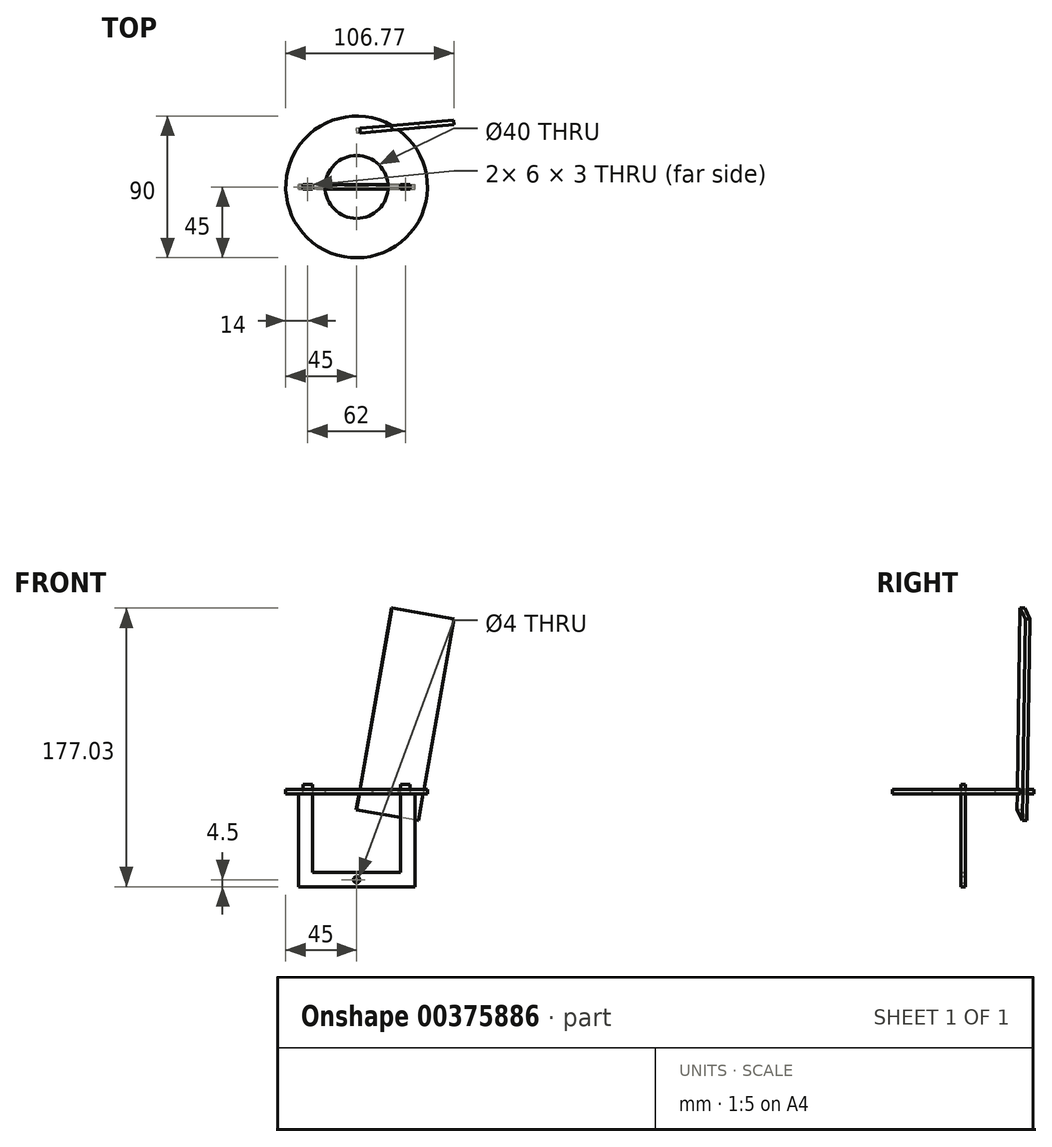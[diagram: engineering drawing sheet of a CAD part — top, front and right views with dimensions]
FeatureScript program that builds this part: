
annotation { "Feature Type Name" : "Feature", "Feature Type Description" : "" }
export const myFeature = defineFeature(function(context is Context, id is Id, definition is map)
    precondition{}
    {
        {
            var Q0;
            Q0=qCreatedBy(makeId("Top.planeOp"),FACE);
            var sketch = newSketch(context, id + "F0", { "sketchPlane" : qUnion([Q0])});
            skCircle(sketch, "E0", {"center": v(0, 0) * mm, "radius": 20 * mm});
            skCircle(sketch, "E1", {"center": v(0, 0) * mm, "radius": 45 * mm});
            skLineSegment(sketch, "E2.bottom", {"start": v(-34, -1.5) * mm, "end": v(-28, -1.5) * mm});
            skLineSegment(sketch, "E2.top", {"start": v(-34, 1.5) * mm, "end": v(-28, 1.5) * mm});
            skLineSegment(sketch, "E2.left", {"start": v(-34, -1.5) * mm, "end": v(-34, 1.5) * mm});
            skLineSegment(sketch, "E2.right", {"start": v(-28, -1.5) * mm, "end": v(-28, 1.5) * mm});
            skPoint(sketch, "E2.middle", {"position": v(-31, 0) * mm});
            skLineSegment(sketch, "E3.MirrorCS", {"start": v(34, -1.5) * mm, "end": v(28, -1.5) * mm});
            skPoint(sketch, "E4.MirrorP", {"position": v(31, 0) * mm});
            skLineSegment(sketch, "E5.MirrorCS", {"start": v(34, -1.5) * mm, "end": v(34, 1.5) * mm});
            skLineSegment(sketch, "E6.MirrorCS", {"start": v(34, 1.5) * mm, "end": v(28, 1.5) * mm});
            skLineSegment(sketch, "E7.MirrorCS", {"start": v(28, -1.5) * mm, "end": v(28, 1.5) * mm});
            skSolve(sketch);
        }
        {
            var Q0;
            Q0=makeQuery(id+"F0.imprint","IMPRINT",FACE,{"disambiguationData":[TD([[makeQuery(id+"F0.imprint","IMPRINT",EDGE,{"derivedFrom":sQuery(id+"F0.wireOp",EDGE,"E0")}),-1.0]])]});
            extrude(context, id + "F1", {"entities" : qUnion([Q0]), "depth" : 3 * mm});
        }
        {
            var Q0;
            Q0=qCreatedBy(makeId("Top.planeOp"),FACE);
            var sketch = newSketch(context, id + "F2", { "sketchPlane" : qUnion([Q0])});
            skLineSegment(sketch, "E8", {"start": v(9.74, 37.99) * mm, "end": v(39.62, 40.6) * mm});
            skLineSegment(sketch, "E9", {"start": v(39.62, 40.6) * mm, "end": v(39.89, 37.61) * mm});
            skLineSegment(sketch, "E10", {"start": v(39.89, 37.61) * mm, "end": v(10, 35) * mm});
            skLineSegment(sketch, "E11", {"start": v(9.74, 37.99) * mm, "end": v(10, 35) * mm});
            skCircle(sketch, "E12.0", {"center": v(0, 0) * mm, "radius": 20 * mm, "construction": true});
            skSolve(sketch);
        }
        {
            var Q0;
            Q0=makeQuery(id+"F2.imprint","IMPRINT",FACE,{"disambiguationData":[TD([[makeQuery(id+"F2.imprint","IMPRINT",EDGE,{"derivedFrom":sQuery(id+"F2.wireOp",EDGE,"E8")}),-1.0]])]});
            extrude(context, id + "F3", {"entities" : qUnion([Q0]), "operationType" : NewBodyOperationType.REMOVE, "depth" : 25 * mm});
        }
        {
            var Q0;
            Q0=makeQuery(id+"F3.boolean.opBoolean","COPY",FACE,{"derivedFrom":makeQuery(id+"F3.opExtrude","SWEPT_FACE",FACE,{"disambiguationData":[OSD([sQuery(id+"F2.wireOp",EDGE,"E10")])]})});
            var sketch = newSketch(context, id + "F4", { "sketchPlane" : qUnion([Q0])});
            skLineSegment(sketch, "E13.bottom", {"start": v(-64.98, 111.08) * mm, "end": v(-25.59, 118.03) * mm});
            skLineSegment(sketch, "E13.top", {"start": v(-42.4, -16.95) * mm, "end": v(-3.01, -10) * mm});
            skLineSegment(sketch, "E13.left", {"start": v(-64.98, 111.08) * mm, "end": v(-42.4, -16.95) * mm});
            skLineSegment(sketch, "E13.right", {"start": v(-25.59, 118.03) * mm, "end": v(-5.3, 3) * mm});
            skLineSegment(sketch, "E14.0", {"start": v(-13.01, 3) * mm, "end": v(-13.01, 0) * mm});
            skLineSegment(sketch, "E15", {"start": v(-13.01, 0) * mm, "end": v(-4.78, 0) * mm});
            skLineSegment(sketch, "E16", {"start": v(-13.01, 3) * mm, "end": v(-5.3, 3) * mm});
            skLineSegment(sketch, "E17.trimOffspring", {"start": v(-4.78, 0) * mm, "end": v(-3.01, -10) * mm});
            skPoint(sketch, "E18", {"position": v(-13.01, -11.76) * mm});
            skSolve(sketch);
        }
        {
            var Q0;
            Q0 = qSketchRegion(id + "F4", true);
            var Q1;
            Q1=makeQuery(id+"F3.boolean.opBoolean","COPY",FACE,{"derivedFrom":makeQuery(id+"F3.opExtrude","SWEPT_FACE",FACE,{"disambiguationData":[OSD([sQuery(id+"F2.wireOp",EDGE,"E8")])]})});
            extrude(context, id + "F5", {"entities" : qUnion([Q0]), "endBoundEntityFace" : qUnion([Q1]), "depth" : 3 * mm});
        }
        {
            var Q0;
            Q0=qCreatedBy(makeId("Front.planeOp"),FACE);
            var sketch = newSketch(context, id + "F6", { "sketchPlane" : qUnion([Q0])});
            skLineSegment(sketch, "E19.0", {"start": v(-34, 3) * mm, "end": v(-34, 0) * mm});
            skLineSegment(sketch, "E20.0", {"start": v(-28, 3) * mm, "end": v(-28, 0) * mm});
            skLineSegment(sketch, "E21", {"start": v(-28, 3) * mm, "end": v(-28, 6) * mm});
            skLineSegment(sketch, "E22", {"start": v(-28, 6) * mm, "end": v(-34, 6) * mm});
            skLineSegment(sketch, "E23", {"start": v(-34, 3) * mm, "end": v(-34, 6) * mm});
            skLineSegment(sketch, "E24", {"start": v(-28, 0) * mm, "end": v(-28, -50) * mm});
            skLineSegment(sketch, "E25", {"start": v(-34, 0) * mm, "end": v(-37, 0) * mm});
            skLineSegment(sketch, "E26", {"start": v(-37, 0) * mm, "end": v(-37, -59) * mm});
            skLineSegment(sketch, "E27.MirrorCS", {"start": v(28, 3) * mm, "end": v(28, 6) * mm});
            skLineSegment(sketch, "E28.MirrorCS", {"start": v(28, 3) * mm, "end": v(28, 0) * mm});
            skLineSegment(sketch, "E29.MirrorCS", {"start": v(34, 3) * mm, "end": v(34, 0) * mm});
            skLineSegment(sketch, "E30.MirrorCS", {"start": v(34, 3) * mm, "end": v(34, 6) * mm});
            skLineSegment(sketch, "E31.MirrorCS", {"start": v(34, 0) * mm, "end": v(37, 0) * mm});
            skLineSegment(sketch, "E32.MirrorCS", {"start": v(28, 6) * mm, "end": v(34, 6) * mm});
            skLineSegment(sketch, "E33.MirrorCS", {"start": v(28, 0) * mm, "end": v(28, -50) * mm});
            skLineSegment(sketch, "E34.MirrorCS", {"start": v(37, 0) * mm, "end": v(37, -59) * mm});
            skLineSegment(sketch, "E35", {"start": v(28, -50) * mm, "end": v(-28, -50) * mm});
            skLineSegment(sketch, "E36", {"start": v(-37, -59) * mm, "end": v(37, -59) * mm});
            skLineSegment(sketch, "E37", {"start": v(0, -50) * mm, "end": v(0, -59) * mm, "construction": true});
            skCircle(sketch, "E38", {"center": v(0, -54.5) * mm, "radius": 2 * mm});
            skSolve(sketch);
        }
        {
            var Q0;
            Q0=makeQuery(id+"F6.imprint","IMPRINT",FACE,{"disambiguationData":[TD([[makeQuery(id+"F6.imprint","IMPRINT",EDGE,{"derivedFrom":sQuery(id+"F6.wireOp",EDGE,"E19.0")}),1.0]])]});
            extrude(context, id + "F7", {"entities" : qUnion([Q0]), "depth" : 3 * mm, "symmetric" : true});
        }
    });
